# Revit family: Haworth_BuzziHood
name_source: partatom
category: Furniture
revit_build: Autodesk Revit 2018 (Build: 20170223_1515(x64)
units: mm (PartAtom-declared; Revit-internal decimal feet)

## family parameters
Always vertical = Yes
Cut with Voids When Loaded = No
Host = Wall
Room Calculation Point = No
Shared = No

## types (6) — shared parameters
Actual Depth = 27 243/256"
Actual Height = 42 33/256"
Actual Width = 35 61/256"
Assembly Code = E2020200
Default Elevation = 48"
Manufacturer = Haworth
Model = HCBZ-HDB1
Mounting Height = 39 47/128"
Revision Number = 1
Size = Verify Final Dim. w/ Haworth
URL = https://www.haworth.com
URL - Product = https://www.haworth.com
Warranty = https://www.haworth.com

## per-type parameters (varying)
| type | 3D | Back Void Length | Description | Flat | No Tablet | Tablet | Void Length | Wood Tablet |
| HCBZ-HDB1-F2 | No | 1/4" | Haworth BuzziHood Wall Mounted Privacy Booth Flat w/o Tablet | Yes | Yes | No | 5" | No |
| HCBZ-HDB1-F2TP | No | 1/4" | Haworth BuzziHood Wall Mounted Privacy Booth Flat w Painted Tablet | Yes | No | Yes | 5" | No |
| HCBZ-HDB1-F2TW | No | 1/4" | Haworth BuzziHood Wall Mounted Privacy Booth Flat w/ Wood Tablet | Yes | No | No | 5" | Yes |
| HCBZ-HDB1-32 | Yes | 2 121/256" | Haworth BuzziHood Wall Mounted Privacy Booth 3D w/o Tablet | No | Yes | No | 42 1/2" | No |
| HCBZ-HDB1-32TP | Yes | 2 121/256" | Haworth BuzziHood Wall Mounted Privacy Booth 3D w Painted Tablet | No | No | Yes | 42 1/2" | No |
| HCBZ-HDB1-32TW | Yes | 2 121/256" | Haworth BuzziHood Wall Mounted Privacy Booth 3D w Wood Tablet | No | No | No | 42 1/2" | Yes |

## geometry (parser evidence)
native form markers: Sweep x1
no freeform markers — native parametric forms only
